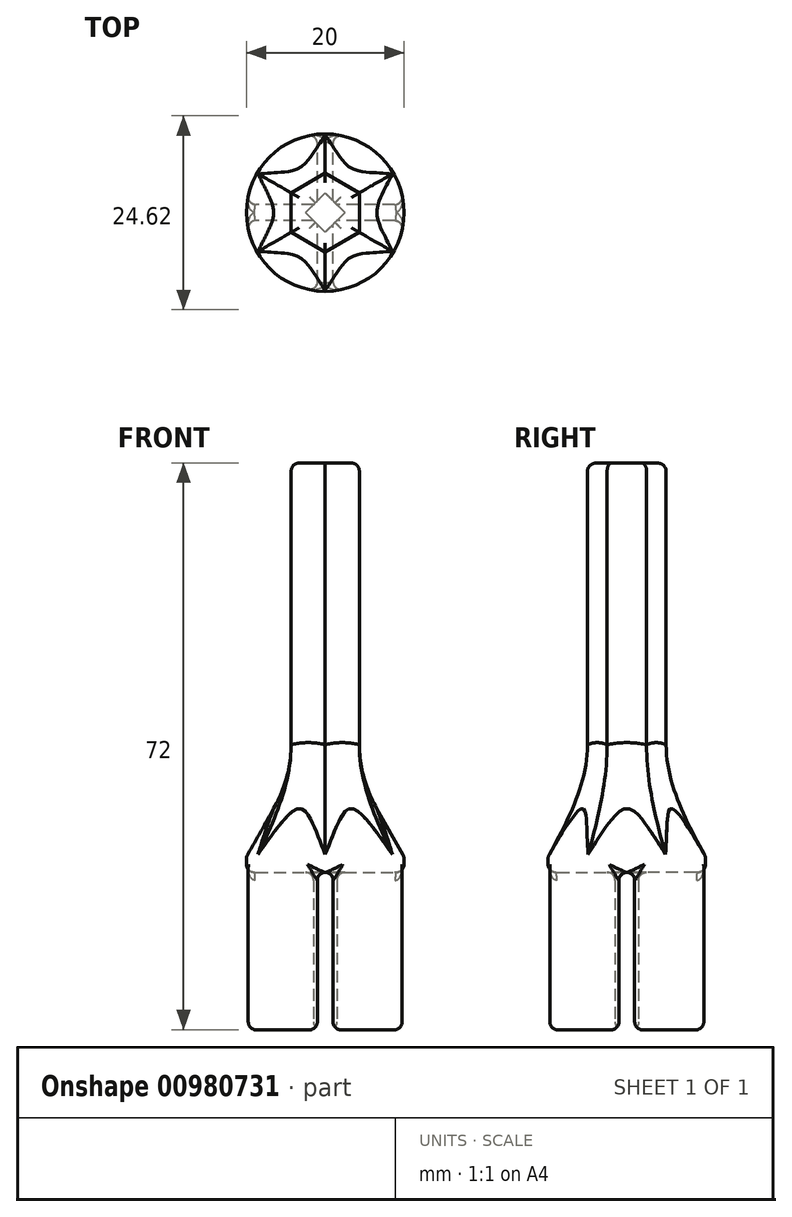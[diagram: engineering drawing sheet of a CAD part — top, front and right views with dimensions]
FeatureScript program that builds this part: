
annotation { "Feature Type Name" : "Feature", "Feature Type Description" : "" }
export const myFeature = defineFeature(function(context is Context, id is Id, definition is map)
    precondition{}
    {
        {
            var Q0;
            Q0=qCreatedBy(makeId("Top.planeOp"),FACE);
            var sketch = newSketch(context, id + "F0", { "sketchPlane" : qUnion([Q0])});
            skCircle(sketch, "E0", {"center": v(0, 0) * mm, "radius": 10 * mm});
            skLineSegment(sketch, "E1.bottom", {"start": v(15, -1) * mm, "end": v(1.5, -1) * mm});
            skLineSegment(sketch, "E1.top", {"start": v(15, 1) * mm, "end": v(1.5, 1) * mm});
            skLineSegment(sketch, "E1.left", {"start": v(15, -1) * mm, "end": v(15, 1) * mm});
            skLineSegment(sketch, "E1.right", {"start": v(-15, -1) * mm, "end": v(-15, 1) * mm});
            skLineSegment(sketch, "E2.bottom", {"start": v(1, -15) * mm, "end": v(-1, -15) * mm});
            skLineSegment(sketch, "E2.top", {"start": v(1, 15) * mm, "end": v(-1, 15) * mm});
            skLineSegment(sketch, "E2.left", {"start": v(1, -15) * mm, "end": v(1, -1.5) * mm});
            skLineSegment(sketch, "E2.right", {"start": v(-1, -15) * mm, "end": v(-1, -1.5) * mm});
            skLineSegment(sketch, "E3.bottom", {"start": v(1.5, -1.5) * mm, "end": v(-1.5, -1.5) * mm, "construction": true});
            skLineSegment(sketch, "E3.top", {"start": v(1.5, 1.5) * mm, "end": v(-1.5, 1.5) * mm, "construction": true});
            skLineSegment(sketch, "E3.left", {"start": v(1.5, -1.5) * mm, "end": v(1.5, 1.5) * mm, "construction": true});
            skLineSegment(sketch, "E3.right", {"start": v(-1.5, -1.5) * mm, "end": v(-1.5, 1.5) * mm, "construction": true});
            skLineSegment(sketch, "E4", {"start": v(1.5, 1) * mm, "end": v(-1.5, 1) * mm, "construction": true});
            skLineSegment(sketch, "E5", {"start": v(1, 1.5) * mm, "end": v(1, 15) * mm});
            skLineSegment(sketch, "E6", {"start": v(-1, 1.5) * mm, "end": v(-1, 15) * mm});
            skLineSegment(sketch, "E7", {"start": v(-1.5, 1) * mm, "end": v(-15, 1) * mm});
            skLineSegment(sketch, "E8", {"start": v(-1.5, -1) * mm, "end": v(-15, -1) * mm});
            skLineSegment(sketch, "E9", {"start": v(-1, -1.5) * mm, "end": v(-1, 1.5) * mm, "construction": true});
            skLineSegment(sketch, "E10", {"start": v(1, -1.5) * mm, "end": v(1, 1.5) * mm, "construction": true});
            skLineSegment(sketch, "E11", {"start": v(1.5, -1) * mm, "end": v(-1.5, -1) * mm, "construction": true});
            skLineSegment(sketch, "E12", {"start": v(-1.5, -1) * mm, "end": v(-1, -1.5) * mm});
            skLineSegment(sketch, "E13", {"start": v(1, -1.5) * mm, "end": v(1.5, -1) * mm});
            skLineSegment(sketch, "E14", {"start": v(1.5, 1) * mm, "end": v(1, 1.5) * mm});
            skLineSegment(sketch, "E15", {"start": v(-1, 1.5) * mm, "end": v(-1.5, 1) * mm});
            skSolve(sketch);
        }
        {
            var Q0;
            {var subQ5=sQuery(id+"F0.wireOp",EDGE,"E13");Q0=makeQuery(id+"F0.imprint","IMPRINT",FACE,{"disambiguationData":[TD([[makeQuery(id+"F0.imprint","IMPRINT",EDGE,{"derivedFrom":subQ5}),-1.0]])]});}
            var Q1;
            {var subQ5=sQuery(id+"F0.wireOp",EDGE,"E14");Q1=makeQuery(id+"F0.imprint","IMPRINT",FACE,{"disambiguationData":[TD([[makeQuery(id+"F0.imprint","IMPRINT",EDGE,{"derivedFrom":subQ5}),-1.0]])]});}
            var Q2;
            {var subQ5=sQuery(id+"F0.wireOp",EDGE,"E15");Q2=makeQuery(id+"F0.imprint","IMPRINT",FACE,{"disambiguationData":[TD([[makeQuery(id+"F0.imprint","IMPRINT",EDGE,{"derivedFrom":subQ5}),-1.0]])]});}
            var Q3;
            {var subQ0=sQuery(id+"F0.wireOp",EDGE,"E12");Q3=makeQuery(id+"F0.imprint","IMPRINT",FACE,{"disambiguationData":[TD([[makeQuery(id+"F0.imprint","IMPRINT",EDGE,{"derivedFrom":subQ0}),1.0]])]});}
            var Q4;
            {var subQ5=sQuery(id+"F0.wireOp",EDGE,"E12");Q4=makeQuery(id+"F0.imprint","IMPRINT",FACE,{"disambiguationData":[TD([[makeQuery(id+"F0.imprint","IMPRINT",EDGE,{"derivedFrom":subQ5}),-1.0]])]});}
            extrude(context, id + "F1", {"entities" : qUnion([Q0, Q1, Q2, Q3, Q4]), "depth" : 22 * mm, "offsetDistance" : 25 * mm});
        }
        {
            var Q0;
            {var subQ5=sQuery(id+"F0.wireOp",EDGE,"E1.left");Q0=makeQuery(id+"F0.imprint","IMPRINT",FACE,{"disambiguationData":[TD([[makeQuery(id+"F0.imprint","IMPRINT",EDGE,{"derivedFrom":subQ5}),1.0]])]});}
            var Q1;
            {var subQ5=sQuery(id+"F0.wireOp",EDGE,"E2.top");Q1=makeQuery(id+"F0.imprint","IMPRINT",FACE,{"disambiguationData":[TD([[makeQuery(id+"F0.imprint","IMPRINT",EDGE,{"derivedFrom":subQ5}),1.0]])]});}
            var Q2;
            {var subQ5=sQuery(id+"F0.wireOp",EDGE,"E1.right");Q2=makeQuery(id+"F0.imprint","IMPRINT",FACE,{"disambiguationData":[TD([[makeQuery(id+"F0.imprint","IMPRINT",EDGE,{"derivedFrom":subQ5}),-1.0]])]});}
            var Q3;
            {var subQ0=sQuery(id+"F0.wireOp",EDGE,"E12");Q3=makeQuery(id+"F0.imprint","IMPRINT",FACE,{"disambiguationData":[TD([[makeQuery(id+"F0.imprint","IMPRINT",EDGE,{"derivedFrom":subQ0}),1.0]])]});}
            var Q4;
            {var subQ5=sQuery(id+"F0.wireOp",EDGE,"E2.bottom");Q4=makeQuery(id+"F0.imprint","IMPRINT",FACE,{"disambiguationData":[TD([[makeQuery(id+"F0.imprint","IMPRINT",EDGE,{"derivedFrom":subQ5}),-1.0]])]});}
            extrude(context, id + "F2", {"entities" : qUnion([Q0, Q1, Q2, Q3, Q4]), "operationType" : NewBodyOperationType.REMOVE, "depth" : 20 * mm, "offsetDistance" : 25 * mm});
        }
        {
            var Q0;
            Q0=qCreatedBy(makeId("Top.planeOp"),FACE);
            cPlane(context, id + "F3", {"entities" : qUnion([Q0]), "cplaneType" : CPlaneType.OFFSET, "offset" : 32 * mm, "width" : 150 * mm, "height" : 150 * mm});
        }
        {
            var Q0;
            Q0=qCreatedBy(id+"F3.planeOp",FACE);
            var sketch = newSketch(context, id + "F4", { "sketchPlane" : qUnion([Q0])});
            skCircle(sketch, "E16.cCircle", {"center": v(0, 0) * mm, "radius": 5 * mm, "construction": true});
            skLineSegment(sketch, "E16.0", {"start": v(0, 5) * mm, "end": v(4.33, 2.5) * mm});
            skLineSegment(sketch, "E16.1", {"start": v(4.33, 2.5) * mm, "end": v(4.33, -2.5) * mm});
            skLineSegment(sketch, "E16.2", {"start": v(4.33, -2.5) * mm, "end": v(0, -5) * mm});
            skLineSegment(sketch, "E16.3", {"start": v(0, -5) * mm, "end": v(-4.33, -2.5) * mm});
            skLineSegment(sketch, "E16.4", {"start": v(-4.33, -2.5) * mm, "end": v(-4.33, 2.5) * mm});
            skLineSegment(sketch, "E16.5", {"start": v(-4.33, 2.5) * mm, "end": v(0, 5) * mm});
            skCircle(sketch, "E17", {"center": v(0, 0) * mm, "radius": 4.33 * mm});
            skSolve(sketch);
        }
        {
            var Q0;
            {var subQ0=sQuery(id+"F4.wireOp",EDGE,"E17");var subQ4=makeQuery(id+"F4.imprint","INTERSECT",VERTEX,{"derivedFrom":[sQuery(id+"F4.wireOp",EDGE,"E16.0"),subQ0]});Q0=makeQuery(id+"F4.imprint","IMPRINT",FACE,{"disambiguationData":[TD([[makeQuery(id+"F4.imprint","IMPRINT",EDGE,{"disambiguationData":[TD([[subQ4,1.0]])],"derivedFrom":subQ0}),1.0]])]});}
            var sketch = newSketch(context, id + "F5", { "sketchPlane" : qUnion([Q0])});
            skSolve(sketch);
        }
        {
            var Q1;
            Q1=makeQuery(id+"F1.opExtrude","CAP_FACE",FACE,{"disambiguationData":[OSD([sQuery(id+"F0.wireOp",EDGE,"E0")])],"isStart":false});
            var Q2;
            {var subQ0=sQuery(id+"F4.wireOp",EDGE,"E17");var subQ4=makeQuery(id+"F4.imprint","INTERSECT",VERTEX,{"derivedFrom":[sQuery(id+"F4.wireOp",EDGE,"E16.0"),subQ0]});Q2=makeQuery(id+"F5.imprint","IMPRINT",FACE,{"disambiguationData":[TD([[makeQuery(id+"F5.imprint","IMPRINT",EDGE,{"derivedFrom":makeQuery(id+"F4.imprint","IMPRINT",EDGE,{"disambiguationData":[TD([[subQ4,1.0]])],"derivedFrom":subQ0})}),1.0]])]});}
            loft(context, id + "F6", {"operationType" : NewBodyOperationType.ADD, "sheetProfilesArray" : [{ "sheetProfileEntities" : qUnion([Q1]) }, { "sheetProfileEntities" : qUnion([Q2]) }]});
        }
        {
            var Q0;
            {var subQ0=sQuery(id+"F4.wireOp",EDGE,"E16.4");var subQ1=sQuery(id+"F4.wireOp",EDGE,"E16.3");var subQ2=makeQuery(id+"F4.imprint","INTERSECT",VERTEX,{"derivedFrom":[subQ1,subQ0]});Q0=makeQuery(id+"F4.imprint","IMPRINT",FACE,{"disambiguationData":[TD([[makeQuery(id+"F4.imprint","IMPRINT",EDGE,{"disambiguationData":[TD([[subQ2,1.0]])],"derivedFrom":subQ1}),-1.0]])]});}
            var Q1;
            {var subQ0=sQuery(id+"F4.wireOp",EDGE,"E16.5");var subQ1=sQuery(id+"F4.wireOp",EDGE,"E16.0");var subQ2=makeQuery(id+"F4.imprint","INTERSECT",VERTEX,{"derivedFrom":[subQ1,subQ0]});Q1=makeQuery(id+"F4.imprint","IMPRINT",FACE,{"disambiguationData":[TD([[makeQuery(id+"F4.imprint","IMPRINT",EDGE,{"disambiguationData":[TD([[subQ2,-1.0]])],"derivedFrom":subQ1}),-1.0]])]});}
            var Q2;
            {var subQ0=sQuery(id+"F4.wireOp",EDGE,"E16.1");var subQ1=sQuery(id+"F4.wireOp",EDGE,"E16.0");var subQ2=makeQuery(id+"F4.imprint","INTERSECT",VERTEX,{"derivedFrom":[subQ1,subQ0]});Q2=makeQuery(id+"F4.imprint","IMPRINT",FACE,{"disambiguationData":[TD([[makeQuery(id+"F4.imprint","IMPRINT",EDGE,{"disambiguationData":[TD([[subQ2,1.0]])],"derivedFrom":subQ1}),-1.0]])]});}
            var Q3;
            {var subQ0=sQuery(id+"F4.wireOp",EDGE,"E16.3");var subQ1=sQuery(id+"F4.wireOp",EDGE,"E16.2");var subQ2=makeQuery(id+"F4.imprint","INTERSECT",VERTEX,{"derivedFrom":[subQ1,subQ0]});Q3=makeQuery(id+"F4.imprint","IMPRINT",FACE,{"disambiguationData":[TD([[makeQuery(id+"F4.imprint","IMPRINT",EDGE,{"disambiguationData":[TD([[subQ2,1.0]])],"derivedFrom":subQ1}),-1.0]])]});}
            var Q4;
            {var subQ0=sQuery(id+"F4.wireOp",EDGE,"E17");var subQ4=makeQuery(id+"F4.imprint","INTERSECT",VERTEX,{"derivedFrom":[sQuery(id+"F4.wireOp",EDGE,"E16.0"),subQ0]});Q4=makeQuery(id+"F4.imprint","IMPRINT",FACE,{"disambiguationData":[TD([[makeQuery(id+"F4.imprint","IMPRINT",EDGE,{"disambiguationData":[TD([[subQ4,1.0]])],"derivedFrom":subQ0}),1.0]])]});}
            var Q5;
            {var subQ0=sQuery(id+"F4.wireOp",EDGE,"E16.2");var subQ1=sQuery(id+"F4.wireOp",EDGE,"E16.1");var subQ2=makeQuery(id+"F4.imprint","INTERSECT",VERTEX,{"derivedFrom":[subQ1,subQ0]});Q5=makeQuery(id+"F4.imprint","IMPRINT",FACE,{"disambiguationData":[TD([[makeQuery(id+"F4.imprint","IMPRINT",EDGE,{"disambiguationData":[TD([[subQ2,1.0]])],"derivedFrom":subQ1}),-1.0]])]});}
            var Q6;
            {var subQ0=sQuery(id+"F4.wireOp",EDGE,"E16.5");var subQ1=sQuery(id+"F4.wireOp",EDGE,"E16.4");var subQ2=makeQuery(id+"F4.imprint","INTERSECT",VERTEX,{"derivedFrom":[subQ1,subQ0]});Q6=makeQuery(id+"F4.imprint","IMPRINT",FACE,{"disambiguationData":[TD([[makeQuery(id+"F4.imprint","IMPRINT",EDGE,{"disambiguationData":[TD([[subQ2,1.0]])],"derivedFrom":subQ1}),-1.0]])]});}
            extrude(context, id + "F7", {"entities" : qUnion([Q0, Q1, Q2, Q3, Q4, Q5, Q6]), "operationType" : NewBodyOperationType.ADD, "depth" : 40 * mm, "offsetDistance" : 25 * mm});
        }
        {
            var Q0;
            {var subQ0=sQuery(id+"F4.wireOp",EDGE,"E16.3");var subQ1=sQuery(id+"F4.wireOp",EDGE,"E16.2");var subQ2=makeQuery(id+"F7.opExtrude","CAP_FACE",FACE,{"disambiguationData":[OSD([sQuery(id+"F4.wireOp",EDGE,"E16.0"),sQuery(id+"F4.wireOp",EDGE,"E16.1"),subQ1,subQ0,sQuery(id+"F4.wireOp",EDGE,"E16.4"),sQuery(id+"F4.wireOp",EDGE,"E16.5")])],"isStart":true});Q0=makeQuery(id+"F7.boolean.opBoolean","SPLIT",FACE,{"disambiguationData":[TD([makeQuery(id+"F6.opLoft","SWEPT_FACE",FACE,{"disambiguationData":[OSD([sQuery(id+"F0.wireOp",EDGE,"E0"),sQuery(id+"F4.wireOp",EDGE,"E17")])]}),subQ2,makeQuery(id+"F7.opExtrude","SWEPT_FACE",FACE,{"disambiguationData":[OSD([subQ1])]}),makeQuery(id+"F7.opExtrude","SWEPT_FACE",FACE,{"disambiguationData":[OSD([subQ0])]})])],"derivedFrom":subQ2});}
            var Q1;
            {var subQ0=sQuery(id+"F4.wireOp",EDGE,"E16.1");var subQ1=sQuery(id+"F4.wireOp",EDGE,"E16.2");var subQ2=makeQuery(id+"F7.opExtrude","CAP_FACE",FACE,{"disambiguationData":[OSD([sQuery(id+"F4.wireOp",EDGE,"E16.0"),subQ0,subQ1,sQuery(id+"F4.wireOp",EDGE,"E16.3"),sQuery(id+"F4.wireOp",EDGE,"E16.4"),sQuery(id+"F4.wireOp",EDGE,"E16.5")])],"isStart":true});Q1=makeQuery(id+"F7.boolean.opBoolean","SPLIT",FACE,{"disambiguationData":[TD([makeQuery(id+"F6.opLoft","SWEPT_FACE",FACE,{"disambiguationData":[OSD([sQuery(id+"F0.wireOp",EDGE,"E0"),sQuery(id+"F4.wireOp",EDGE,"E17")])]}),subQ2,makeQuery(id+"F7.opExtrude","SWEPT_FACE",FACE,{"disambiguationData":[OSD([subQ0])]}),makeQuery(id+"F7.opExtrude","SWEPT_FACE",FACE,{"disambiguationData":[OSD([subQ1])]})])],"derivedFrom":subQ2});}
            var Q2;
            {var subQ0=sQuery(id+"F4.wireOp",EDGE,"E16.4");var subQ1=sQuery(id+"F4.wireOp",EDGE,"E16.3");var subQ2=makeQuery(id+"F7.opExtrude","CAP_FACE",FACE,{"disambiguationData":[OSD([sQuery(id+"F4.wireOp",EDGE,"E16.0"),sQuery(id+"F4.wireOp",EDGE,"E16.1"),sQuery(id+"F4.wireOp",EDGE,"E16.2"),subQ1,subQ0,sQuery(id+"F4.wireOp",EDGE,"E16.5")])],"isStart":true});Q2=makeQuery(id+"F7.boolean.opBoolean","SPLIT",FACE,{"disambiguationData":[TD([makeQuery(id+"F6.opLoft","SWEPT_FACE",FACE,{"disambiguationData":[OSD([sQuery(id+"F0.wireOp",EDGE,"E0"),sQuery(id+"F4.wireOp",EDGE,"E17")])]}),subQ2,makeQuery(id+"F7.opExtrude","SWEPT_FACE",FACE,{"disambiguationData":[OSD([subQ1])]}),makeQuery(id+"F7.opExtrude","SWEPT_FACE",FACE,{"disambiguationData":[OSD([subQ0])]})])],"derivedFrom":subQ2});}
            var Q3;
            {var subQ0=sQuery(id+"F4.wireOp",EDGE,"E16.5");var subQ1=sQuery(id+"F4.wireOp",EDGE,"E16.4");var subQ2=makeQuery(id+"F7.opExtrude","CAP_FACE",FACE,{"disambiguationData":[OSD([sQuery(id+"F4.wireOp",EDGE,"E16.0"),sQuery(id+"F4.wireOp",EDGE,"E16.1"),sQuery(id+"F4.wireOp",EDGE,"E16.2"),sQuery(id+"F4.wireOp",EDGE,"E16.3"),subQ1,subQ0])],"isStart":true});Q3=makeQuery(id+"F7.boolean.opBoolean","SPLIT",FACE,{"disambiguationData":[TD([makeQuery(id+"F6.opLoft","SWEPT_FACE",FACE,{"disambiguationData":[OSD([sQuery(id+"F0.wireOp",EDGE,"E0"),sQuery(id+"F4.wireOp",EDGE,"E17")])]}),subQ2,makeQuery(id+"F7.opExtrude","SWEPT_FACE",FACE,{"disambiguationData":[OSD([subQ1])]}),makeQuery(id+"F7.opExtrude","SWEPT_FACE",FACE,{"disambiguationData":[OSD([subQ0])]})])],"derivedFrom":subQ2});}
            var Q4;
            {var subQ0=sQuery(id+"F4.wireOp",EDGE,"E16.0");var subQ1=sQuery(id+"F4.wireOp",EDGE,"E16.5");var subQ2=makeQuery(id+"F7.opExtrude","CAP_FACE",FACE,{"disambiguationData":[OSD([subQ0,sQuery(id+"F4.wireOp",EDGE,"E16.1"),sQuery(id+"F4.wireOp",EDGE,"E16.2"),sQuery(id+"F4.wireOp",EDGE,"E16.3"),sQuery(id+"F4.wireOp",EDGE,"E16.4"),subQ1])],"isStart":true});Q4=makeQuery(id+"F7.boolean.opBoolean","SPLIT",FACE,{"disambiguationData":[TD([makeQuery(id+"F6.opLoft","SWEPT_FACE",FACE,{"disambiguationData":[OSD([sQuery(id+"F0.wireOp",EDGE,"E0"),sQuery(id+"F4.wireOp",EDGE,"E17")])]}),makeQuery(id+"F7.opExtrude","SWEPT_FACE",FACE,{"disambiguationData":[OSD([subQ0])]}),subQ2,makeQuery(id+"F7.opExtrude","SWEPT_FACE",FACE,{"disambiguationData":[OSD([subQ1])]})])],"derivedFrom":subQ2});}
            var Q5;
            {var subQ0=sQuery(id+"F4.wireOp",EDGE,"E16.1");var subQ1=sQuery(id+"F4.wireOp",EDGE,"E16.0");var subQ2=makeQuery(id+"F7.opExtrude","CAP_FACE",FACE,{"disambiguationData":[OSD([subQ1,subQ0,sQuery(id+"F4.wireOp",EDGE,"E16.2"),sQuery(id+"F4.wireOp",EDGE,"E16.3"),sQuery(id+"F4.wireOp",EDGE,"E16.4"),sQuery(id+"F4.wireOp",EDGE,"E16.5")])],"isStart":true});Q5=makeQuery(id+"F7.boolean.opBoolean","SPLIT",FACE,{"disambiguationData":[TD([makeQuery(id+"F6.opLoft","SWEPT_FACE",FACE,{"disambiguationData":[OSD([sQuery(id+"F0.wireOp",EDGE,"E0"),sQuery(id+"F4.wireOp",EDGE,"E17")])]}),makeQuery(id+"F7.opExtrude","SWEPT_FACE",FACE,{"disambiguationData":[OSD([subQ1])]}),subQ2,makeQuery(id+"F7.opExtrude","SWEPT_FACE",FACE,{"disambiguationData":[OSD([subQ0])]})])],"derivedFrom":subQ2});}
            extrude(context, id + "F8", {"entities" : qUnion([Q0, Q1, Q2, Q3, Q4, Q5]), "operationType" : NewBodyOperationType.ADD, "depth" : 2 * mm, "offsetDistance" : 25 * mm});
        }
        {
            var Q0;
            {var subQ0=makeQuery(id+"F6.opLoft","SWEPT_FACE",FACE,{"disambiguationData":[OSD([sQuery(id+"F0.wireOp",EDGE,"E0"),sQuery(id+"F4.wireOp",EDGE,"E17")])]});var subQ1=sQuery(id+"F4.wireOp",EDGE,"E16.5");var subQ2=sQuery(id+"F4.wireOp",EDGE,"E16.4");var subQ3=sQuery(id+"F4.wireOp",EDGE,"E16.0");var subQ6=makeQuery(id+"F7.opExtrude","CAP_EDGE",EDGE,{"disambiguationData":[OSD([subQ1])],"isStart":true});Q0=makeQuery(id+"F8.boolean.opBoolean","INTERSECT",EDGE,{"derivedFrom":[subQ0,makeQuery(id+"F8.opExtrude","SWEPT_FACE",FACE,{"disambiguationData":[OSD([subQ1]),TDD([makeQuery(id+"F7.boolean.opBoolean","SPLIT",EDGE,{"disambiguationData":[TD([makeQuery(id+"F7.opExtrude","SWEPT_FACE",FACE,{"disambiguationData":[OSD([subQ3])]})])],"derivedFrom":subQ6})])]}),makeQuery(id+"F8.opExtrude","SWEPT_FACE",FACE,{"disambiguationData":[OSD([subQ1]),TDD([makeQuery(id+"F7.boolean.opBoolean","SPLIT",EDGE,{"disambiguationData":[TD([makeQuery(id+"F7.opExtrude","SWEPT_FACE",FACE,{"disambiguationData":[OSD([subQ2])]})])],"derivedFrom":subQ6})])]})]});}
            var Q1;
            {var subQ0=makeQuery(id+"F6.opLoft","SWEPT_FACE",FACE,{"disambiguationData":[OSD([sQuery(id+"F0.wireOp",EDGE,"E0"),sQuery(id+"F4.wireOp",EDGE,"E17")])]});var subQ1=sQuery(id+"F4.wireOp",EDGE,"E16.5");var subQ2=sQuery(id+"F4.wireOp",EDGE,"E16.4");var subQ3=sQuery(id+"F4.wireOp",EDGE,"E16.3");var subQ6=makeQuery(id+"F7.opExtrude","CAP_EDGE",EDGE,{"disambiguationData":[OSD([subQ2])],"isStart":true});Q1=makeQuery(id+"F8.boolean.opBoolean","INTERSECT",EDGE,{"derivedFrom":[subQ0,makeQuery(id+"F8.opExtrude","SWEPT_FACE",FACE,{"disambiguationData":[OSD([subQ2]),TDD([makeQuery(id+"F7.boolean.opBoolean","SPLIT",EDGE,{"disambiguationData":[TD([makeQuery(id+"F7.opExtrude","SWEPT_FACE",FACE,{"disambiguationData":[OSD([subQ3])]})])],"derivedFrom":subQ6})])]}),makeQuery(id+"F8.opExtrude","SWEPT_FACE",FACE,{"disambiguationData":[OSD([subQ2]),TDD([makeQuery(id+"F7.boolean.opBoolean","SPLIT",EDGE,{"disambiguationData":[TD([makeQuery(id+"F7.opExtrude","SWEPT_FACE",FACE,{"disambiguationData":[OSD([subQ1])]})])],"derivedFrom":subQ6})])]})]});}
            var Q2;
            {var subQ0=makeQuery(id+"F6.opLoft","SWEPT_FACE",FACE,{"disambiguationData":[OSD([sQuery(id+"F0.wireOp",EDGE,"E0"),sQuery(id+"F4.wireOp",EDGE,"E17")])]});var subQ1=sQuery(id+"F4.wireOp",EDGE,"E16.3");var subQ2=sQuery(id+"F4.wireOp",EDGE,"E16.2");var subQ3=sQuery(id+"F4.wireOp",EDGE,"E16.1");var subQ6=makeQuery(id+"F7.opExtrude","CAP_EDGE",EDGE,{"disambiguationData":[OSD([subQ2])],"isStart":true});Q2=makeQuery(id+"F8.boolean.opBoolean","INTERSECT",EDGE,{"derivedFrom":[subQ0,makeQuery(id+"F8.opExtrude","SWEPT_FACE",FACE,{"disambiguationData":[OSD([subQ2]),TDD([makeQuery(id+"F7.boolean.opBoolean","SPLIT",EDGE,{"disambiguationData":[TD([makeQuery(id+"F7.opExtrude","SWEPT_FACE",FACE,{"disambiguationData":[OSD([subQ3])]})])],"derivedFrom":subQ6})])]}),makeQuery(id+"F8.opExtrude","SWEPT_FACE",FACE,{"disambiguationData":[OSD([subQ2]),TDD([makeQuery(id+"F7.boolean.opBoolean","SPLIT",EDGE,{"disambiguationData":[TD([makeQuery(id+"F7.opExtrude","SWEPT_FACE",FACE,{"disambiguationData":[OSD([subQ1])]})])],"derivedFrom":subQ6})])]})]});}
            var Q3;
            {var subQ0=makeQuery(id+"F6.opLoft","SWEPT_FACE",FACE,{"disambiguationData":[OSD([sQuery(id+"F0.wireOp",EDGE,"E0"),sQuery(id+"F4.wireOp",EDGE,"E17")])]});var subQ1=sQuery(id+"F4.wireOp",EDGE,"E16.1");var subQ2=sQuery(id+"F4.wireOp",EDGE,"E16.0");var subQ4=sQuery(id+"F4.wireOp",EDGE,"E16.5");var subQ6=makeQuery(id+"F7.opExtrude","CAP_EDGE",EDGE,{"disambiguationData":[OSD([subQ2])],"isStart":true});Q3=makeQuery(id+"F8.boolean.opBoolean","INTERSECT",EDGE,{"derivedFrom":[subQ0,makeQuery(id+"F8.opExtrude","SWEPT_FACE",FACE,{"disambiguationData":[OSD([subQ2]),TDD([makeQuery(id+"F7.boolean.opBoolean","SPLIT",EDGE,{"disambiguationData":[TD([makeQuery(id+"F7.opExtrude","SWEPT_FACE",FACE,{"disambiguationData":[OSD([subQ4])]})])],"derivedFrom":subQ6})])]}),makeQuery(id+"F8.opExtrude","SWEPT_FACE",FACE,{"disambiguationData":[OSD([subQ2]),TDD([makeQuery(id+"F7.boolean.opBoolean","SPLIT",EDGE,{"disambiguationData":[TD([makeQuery(id+"F7.opExtrude","SWEPT_FACE",FACE,{"disambiguationData":[OSD([subQ1])]})])],"derivedFrom":subQ6})])]})]});}
            var Q4;
            {var subQ0=makeQuery(id+"F6.opLoft","SWEPT_FACE",FACE,{"disambiguationData":[OSD([sQuery(id+"F0.wireOp",EDGE,"E0"),sQuery(id+"F4.wireOp",EDGE,"E17")])]});var subQ1=sQuery(id+"F4.wireOp",EDGE,"E16.1");var subQ3=sQuery(id+"F4.wireOp",EDGE,"E16.2");var subQ4=sQuery(id+"F4.wireOp",EDGE,"E16.0");var subQ6=makeQuery(id+"F7.opExtrude","CAP_EDGE",EDGE,{"disambiguationData":[OSD([subQ1])],"isStart":true});Q4=makeQuery(id+"F8.boolean.opBoolean","INTERSECT",EDGE,{"derivedFrom":[subQ0,makeQuery(id+"F8.opExtrude","SWEPT_FACE",FACE,{"disambiguationData":[OSD([subQ1]),TDD([makeQuery(id+"F7.boolean.opBoolean","SPLIT",EDGE,{"disambiguationData":[TD([makeQuery(id+"F7.opExtrude","SWEPT_FACE",FACE,{"disambiguationData":[OSD([subQ4])]})])],"derivedFrom":subQ6})])]}),makeQuery(id+"F8.opExtrude","SWEPT_FACE",FACE,{"disambiguationData":[OSD([subQ1]),TDD([makeQuery(id+"F7.boolean.opBoolean","SPLIT",EDGE,{"disambiguationData":[TD([makeQuery(id+"F7.opExtrude","SWEPT_FACE",FACE,{"disambiguationData":[OSD([subQ3])]})])],"derivedFrom":subQ6})])]})]});}
            var Q5;
            {var subQ0=makeQuery(id+"F6.opLoft","SWEPT_FACE",FACE,{"disambiguationData":[OSD([sQuery(id+"F0.wireOp",EDGE,"E0"),sQuery(id+"F4.wireOp",EDGE,"E17")])]});var subQ1=sQuery(id+"F4.wireOp",EDGE,"E16.4");var subQ2=sQuery(id+"F4.wireOp",EDGE,"E16.3");var subQ3=sQuery(id+"F4.wireOp",EDGE,"E16.2");var subQ6=makeQuery(id+"F7.opExtrude","CAP_EDGE",EDGE,{"disambiguationData":[OSD([subQ2])],"isStart":true});Q5=makeQuery(id+"F8.boolean.opBoolean","INTERSECT",EDGE,{"derivedFrom":[subQ0,makeQuery(id+"F8.opExtrude","SWEPT_FACE",FACE,{"disambiguationData":[OSD([subQ2]),TDD([makeQuery(id+"F7.boolean.opBoolean","SPLIT",EDGE,{"disambiguationData":[TD([makeQuery(id+"F7.opExtrude","SWEPT_FACE",FACE,{"disambiguationData":[OSD([subQ3])]})])],"derivedFrom":subQ6})])]}),makeQuery(id+"F8.opExtrude","SWEPT_FACE",FACE,{"disambiguationData":[OSD([subQ2]),TDD([makeQuery(id+"F7.boolean.opBoolean","SPLIT",EDGE,{"disambiguationData":[TD([makeQuery(id+"F7.opExtrude","SWEPT_FACE",FACE,{"disambiguationData":[OSD([subQ1])]})])],"derivedFrom":subQ6})])]})]});}
            fillet(context, id + "F9", {"entities" : qUnion([Q0, Q1, Q2, Q3, Q4, Q5]), "radius" : 17 * mm, "tangentPropagation" : true, "allowEdgeOverflow" : false});
        }
        {
            var Q0;
            {var subQ0=sQuery(id+"F0.wireOp",EDGE,"E0");Q0=makeQuery(id+"F2.boolean.opBoolean","SPLIT",FACE,{"disambiguationData":[TD([makeQuery(id+"F2.opExtrude","SWEPT_FACE",FACE,{"disambiguationData":[OSD([sQuery(id+"F0.wireOp",EDGE,"E1.bottom")])]})])],"derivedFrom":makeQuery(id+"F1.opExtrude","CAP_FACE",FACE,{"disambiguationData":[OSD([subQ0])],"isStart":true})});}
            var Q1;
            {var subQ0=sQuery(id+"F0.wireOp",EDGE,"E0");Q1=makeQuery(id+"F2.boolean.opBoolean","SPLIT",FACE,{"disambiguationData":[TD([makeQuery(id+"F2.opExtrude","SWEPT_FACE",FACE,{"disambiguationData":[OSD([sQuery(id+"F0.wireOp",EDGE,"E1.top")])]})])],"derivedFrom":makeQuery(id+"F1.opExtrude","CAP_FACE",FACE,{"disambiguationData":[OSD([subQ0])],"isStart":true})});}
            var Q2;
            {var subQ0=sQuery(id+"F0.wireOp",EDGE,"E0");Q2=makeQuery(id+"F2.boolean.opBoolean","SPLIT",FACE,{"disambiguationData":[TD([makeQuery(id+"F2.opExtrude","SWEPT_FACE",FACE,{"disambiguationData":[OSD([sQuery(id+"F0.wireOp",EDGE,"E6")])]})])],"derivedFrom":makeQuery(id+"F1.opExtrude","CAP_FACE",FACE,{"disambiguationData":[OSD([subQ0])],"isStart":true})});}
            var Q3;
            {var subQ0=sQuery(id+"F0.wireOp",EDGE,"E0");Q3=makeQuery(id+"F2.boolean.opBoolean","SPLIT",FACE,{"disambiguationData":[TD([makeQuery(id+"F2.opExtrude","SWEPT_FACE",FACE,{"disambiguationData":[OSD([sQuery(id+"F0.wireOp",EDGE,"E2.right")])]})])],"derivedFrom":makeQuery(id+"F1.opExtrude","CAP_FACE",FACE,{"disambiguationData":[OSD([subQ0])],"isStart":true})});}
            var Q4;
            Q4=makeQuery(id+"F1.opExtrude","SWEPT_FACE",FACE,{"disambiguationData":[OSD([sQuery(id+"F0.wireOp",EDGE,"E0")])]});
            fillet(context, id + "F10", {"entities" : qUnion([Q0, Q1, Q2, Q3, Q4]), "radius" : 1 * mm, "tangentPropagation" : true, "allowEdgeOverflow" : false});
        }
        {
            var Q0;
            {var subQ0=sQuery(id+"F0.wireOp",EDGE,"E6");var subQ1=makeQuery(id+"F1.opExtrude","SWEPT_FACE",FACE,{"disambiguationData":[OSD([sQuery(id+"F0.wireOp",EDGE,"E0")])]});Q0=makeQuery(id+"F10.opFillet","BLEND_EDGE",EDGE,{"blendedFrom":[makeQuery(id+"F2.boolean.opBoolean","INTERSECT",EDGE,{"derivedFrom":[subQ1,makeQuery(id+"F2.opExtrude","SWEPT_FACE",FACE,{"disambiguationData":[OSD([subQ0])]})]}),makeQuery(id+"F2.boolean.opBoolean","INTERSECT",EDGE,{"disambiguationData":[OD(2.0)],"derivedFrom":[subQ1,makeQuery(id+"F2.opExtrude","CAP_FACE",FACE,{"disambiguationData":[OSD([sQuery(id+"F0.wireOp",EDGE,"E1.bottom"),sQuery(id+"F0.wireOp",EDGE,"E1.top"),sQuery(id+"F0.wireOp",EDGE,"E1.left"),sQuery(id+"F0.wireOp",EDGE,"E1.right"),sQuery(id+"F0.wireOp",EDGE,"E2.bottom"),sQuery(id+"F0.wireOp",EDGE,"E2.top"),sQuery(id+"F0.wireOp",EDGE,"E2.left"),sQuery(id+"F0.wireOp",EDGE,"E2.right"),sQuery(id+"F0.wireOp",EDGE,"E5"),subQ0,sQuery(id+"F0.wireOp",EDGE,"E7"),sQuery(id+"F0.wireOp",EDGE,"E8"),sQuery(id+"F0.wireOp",EDGE,"E12"),sQuery(id+"F0.wireOp",EDGE,"E13"),sQuery(id+"F0.wireOp",EDGE,"E14"),sQuery(id+"F0.wireOp",EDGE,"E15")])],"isStart":false})]})],"blendedInto":[]});}
            var Q1;
            {var subQ0=sQuery(id+"F0.wireOp",EDGE,"E5");var subQ1=makeQuery(id+"F1.opExtrude","SWEPT_FACE",FACE,{"disambiguationData":[OSD([sQuery(id+"F0.wireOp",EDGE,"E0")])]});Q1=makeQuery(id+"F10.opFillet","BLEND_EDGE",EDGE,{"blendedFrom":[makeQuery(id+"F2.boolean.opBoolean","INTERSECT",EDGE,{"derivedFrom":[subQ1,makeQuery(id+"F2.opExtrude","SWEPT_FACE",FACE,{"disambiguationData":[OSD([subQ0])]})]}),makeQuery(id+"F2.boolean.opBoolean","INTERSECT",EDGE,{"disambiguationData":[OD(2.0)],"derivedFrom":[subQ1,makeQuery(id+"F2.opExtrude","CAP_FACE",FACE,{"disambiguationData":[OSD([sQuery(id+"F0.wireOp",EDGE,"E1.bottom"),sQuery(id+"F0.wireOp",EDGE,"E1.top"),sQuery(id+"F0.wireOp",EDGE,"E1.left"),sQuery(id+"F0.wireOp",EDGE,"E1.right"),sQuery(id+"F0.wireOp",EDGE,"E2.bottom"),sQuery(id+"F0.wireOp",EDGE,"E2.top"),sQuery(id+"F0.wireOp",EDGE,"E2.left"),sQuery(id+"F0.wireOp",EDGE,"E2.right"),subQ0,sQuery(id+"F0.wireOp",EDGE,"E6"),sQuery(id+"F0.wireOp",EDGE,"E7"),sQuery(id+"F0.wireOp",EDGE,"E8"),sQuery(id+"F0.wireOp",EDGE,"E12"),sQuery(id+"F0.wireOp",EDGE,"E13"),sQuery(id+"F0.wireOp",EDGE,"E14"),sQuery(id+"F0.wireOp",EDGE,"E15")])],"isStart":false})]})],"blendedInto":[]});}
            var Q2;
            {var subQ0=sQuery(id+"F0.wireOp",EDGE,"E1.bottom");var subQ1=makeQuery(id+"F1.opExtrude","SWEPT_FACE",FACE,{"disambiguationData":[OSD([sQuery(id+"F0.wireOp",EDGE,"E0")])]});Q2=makeQuery(id+"F10.opFillet","BLEND_EDGE",EDGE,{"blendedFrom":[makeQuery(id+"F2.boolean.opBoolean","INTERSECT",EDGE,{"derivedFrom":[subQ1,makeQuery(id+"F2.opExtrude","SWEPT_FACE",FACE,{"disambiguationData":[OSD([subQ0])]})]}),makeQuery(id+"F2.boolean.opBoolean","INTERSECT",EDGE,{"disambiguationData":[OD(0.0)],"derivedFrom":[subQ1,makeQuery(id+"F2.opExtrude","CAP_FACE",FACE,{"disambiguationData":[OSD([subQ0,sQuery(id+"F0.wireOp",EDGE,"E1.top"),sQuery(id+"F0.wireOp",EDGE,"E1.left"),sQuery(id+"F0.wireOp",EDGE,"E1.right"),sQuery(id+"F0.wireOp",EDGE,"E2.bottom"),sQuery(id+"F0.wireOp",EDGE,"E2.top"),sQuery(id+"F0.wireOp",EDGE,"E2.left"),sQuery(id+"F0.wireOp",EDGE,"E2.right"),sQuery(id+"F0.wireOp",EDGE,"E5"),sQuery(id+"F0.wireOp",EDGE,"E6"),sQuery(id+"F0.wireOp",EDGE,"E7"),sQuery(id+"F0.wireOp",EDGE,"E8"),sQuery(id+"F0.wireOp",EDGE,"E12"),sQuery(id+"F0.wireOp",EDGE,"E13"),sQuery(id+"F0.wireOp",EDGE,"E14"),sQuery(id+"F0.wireOp",EDGE,"E15")])],"isStart":false})]})],"blendedInto":[]});}
            var Q3;
            {var subQ0=sQuery(id+"F0.wireOp",EDGE,"E1.top");var subQ1=makeQuery(id+"F1.opExtrude","SWEPT_FACE",FACE,{"disambiguationData":[OSD([sQuery(id+"F0.wireOp",EDGE,"E0")])]});Q3=makeQuery(id+"F10.opFillet","BLEND_EDGE",EDGE,{"blendedFrom":[makeQuery(id+"F2.boolean.opBoolean","INTERSECT",EDGE,{"derivedFrom":[subQ1,makeQuery(id+"F2.opExtrude","SWEPT_FACE",FACE,{"disambiguationData":[OSD([subQ0])]})]}),makeQuery(id+"F2.boolean.opBoolean","INTERSECT",EDGE,{"disambiguationData":[OD(0.0)],"derivedFrom":[subQ1,makeQuery(id+"F2.opExtrude","CAP_FACE",FACE,{"disambiguationData":[OSD([sQuery(id+"F0.wireOp",EDGE,"E1.bottom"),subQ0,sQuery(id+"F0.wireOp",EDGE,"E1.left"),sQuery(id+"F0.wireOp",EDGE,"E1.right"),sQuery(id+"F0.wireOp",EDGE,"E2.bottom"),sQuery(id+"F0.wireOp",EDGE,"E2.top"),sQuery(id+"F0.wireOp",EDGE,"E2.left"),sQuery(id+"F0.wireOp",EDGE,"E2.right"),sQuery(id+"F0.wireOp",EDGE,"E5"),sQuery(id+"F0.wireOp",EDGE,"E6"),sQuery(id+"F0.wireOp",EDGE,"E7"),sQuery(id+"F0.wireOp",EDGE,"E8"),sQuery(id+"F0.wireOp",EDGE,"E12"),sQuery(id+"F0.wireOp",EDGE,"E13"),sQuery(id+"F0.wireOp",EDGE,"E14"),sQuery(id+"F0.wireOp",EDGE,"E15")])],"isStart":false})]})],"blendedInto":[]});}
            var Q4;
            {var subQ0=sQuery(id+"F0.wireOp",EDGE,"E2.left");var subQ1=makeQuery(id+"F1.opExtrude","SWEPT_FACE",FACE,{"disambiguationData":[OSD([sQuery(id+"F0.wireOp",EDGE,"E0")])]});Q4=makeQuery(id+"F10.opFillet","BLEND_EDGE",EDGE,{"blendedFrom":[makeQuery(id+"F2.boolean.opBoolean","INTERSECT",EDGE,{"derivedFrom":[subQ1,makeQuery(id+"F2.opExtrude","SWEPT_FACE",FACE,{"disambiguationData":[OSD([subQ0])]})]}),makeQuery(id+"F2.boolean.opBoolean","INTERSECT",EDGE,{"disambiguationData":[OD(1.0)],"derivedFrom":[subQ1,makeQuery(id+"F2.opExtrude","CAP_FACE",FACE,{"disambiguationData":[OSD([sQuery(id+"F0.wireOp",EDGE,"E1.bottom"),sQuery(id+"F0.wireOp",EDGE,"E1.top"),sQuery(id+"F0.wireOp",EDGE,"E1.left"),sQuery(id+"F0.wireOp",EDGE,"E1.right"),sQuery(id+"F0.wireOp",EDGE,"E2.bottom"),sQuery(id+"F0.wireOp",EDGE,"E2.top"),subQ0,sQuery(id+"F0.wireOp",EDGE,"E2.right"),sQuery(id+"F0.wireOp",EDGE,"E5"),sQuery(id+"F0.wireOp",EDGE,"E6"),sQuery(id+"F0.wireOp",EDGE,"E7"),sQuery(id+"F0.wireOp",EDGE,"E8"),sQuery(id+"F0.wireOp",EDGE,"E12"),sQuery(id+"F0.wireOp",EDGE,"E13"),sQuery(id+"F0.wireOp",EDGE,"E14"),sQuery(id+"F0.wireOp",EDGE,"E15")])],"isStart":false})]})],"blendedInto":[]});}
            var Q5;
            {var subQ0=sQuery(id+"F0.wireOp",EDGE,"E2.right");var subQ1=makeQuery(id+"F1.opExtrude","SWEPT_FACE",FACE,{"disambiguationData":[OSD([sQuery(id+"F0.wireOp",EDGE,"E0")])]});Q5=makeQuery(id+"F10.opFillet","BLEND_EDGE",EDGE,{"blendedFrom":[makeQuery(id+"F2.boolean.opBoolean","INTERSECT",EDGE,{"derivedFrom":[subQ1,makeQuery(id+"F2.opExtrude","SWEPT_FACE",FACE,{"disambiguationData":[OSD([subQ0])]})]}),makeQuery(id+"F2.boolean.opBoolean","INTERSECT",EDGE,{"disambiguationData":[OD(1.0)],"derivedFrom":[subQ1,makeQuery(id+"F2.opExtrude","CAP_FACE",FACE,{"disambiguationData":[OSD([sQuery(id+"F0.wireOp",EDGE,"E1.bottom"),sQuery(id+"F0.wireOp",EDGE,"E1.top"),sQuery(id+"F0.wireOp",EDGE,"E1.left"),sQuery(id+"F0.wireOp",EDGE,"E1.right"),sQuery(id+"F0.wireOp",EDGE,"E2.bottom"),sQuery(id+"F0.wireOp",EDGE,"E2.top"),sQuery(id+"F0.wireOp",EDGE,"E2.left"),subQ0,sQuery(id+"F0.wireOp",EDGE,"E5"),sQuery(id+"F0.wireOp",EDGE,"E6"),sQuery(id+"F0.wireOp",EDGE,"E7"),sQuery(id+"F0.wireOp",EDGE,"E8"),sQuery(id+"F0.wireOp",EDGE,"E12"),sQuery(id+"F0.wireOp",EDGE,"E13"),sQuery(id+"F0.wireOp",EDGE,"E14"),sQuery(id+"F0.wireOp",EDGE,"E15")])],"isStart":false})]})],"blendedInto":[]});}
            var Q6;
            {var subQ0=sQuery(id+"F0.wireOp",EDGE,"E8");var subQ1=makeQuery(id+"F1.opExtrude","SWEPT_FACE",FACE,{"disambiguationData":[OSD([sQuery(id+"F0.wireOp",EDGE,"E0")])]});Q6=makeQuery(id+"F10.opFillet","BLEND_EDGE",EDGE,{"blendedFrom":[makeQuery(id+"F2.boolean.opBoolean","INTERSECT",EDGE,{"derivedFrom":[subQ1,makeQuery(id+"F2.opExtrude","SWEPT_FACE",FACE,{"disambiguationData":[OSD([subQ0])]})]}),makeQuery(id+"F2.boolean.opBoolean","INTERSECT",EDGE,{"disambiguationData":[OD(3.0)],"derivedFrom":[subQ1,makeQuery(id+"F2.opExtrude","CAP_FACE",FACE,{"disambiguationData":[OSD([sQuery(id+"F0.wireOp",EDGE,"E1.bottom"),sQuery(id+"F0.wireOp",EDGE,"E1.top"),sQuery(id+"F0.wireOp",EDGE,"E1.left"),sQuery(id+"F0.wireOp",EDGE,"E1.right"),sQuery(id+"F0.wireOp",EDGE,"E2.bottom"),sQuery(id+"F0.wireOp",EDGE,"E2.top"),sQuery(id+"F0.wireOp",EDGE,"E2.left"),sQuery(id+"F0.wireOp",EDGE,"E2.right"),sQuery(id+"F0.wireOp",EDGE,"E5"),sQuery(id+"F0.wireOp",EDGE,"E6"),sQuery(id+"F0.wireOp",EDGE,"E7"),subQ0,sQuery(id+"F0.wireOp",EDGE,"E12"),sQuery(id+"F0.wireOp",EDGE,"E13"),sQuery(id+"F0.wireOp",EDGE,"E14"),sQuery(id+"F0.wireOp",EDGE,"E15")])],"isStart":false})]})],"blendedInto":[]});}
            var Q7;
            {var subQ0=sQuery(id+"F0.wireOp",EDGE,"E7");var subQ1=makeQuery(id+"F1.opExtrude","SWEPT_FACE",FACE,{"disambiguationData":[OSD([sQuery(id+"F0.wireOp",EDGE,"E0")])]});Q7=makeQuery(id+"F10.opFillet","BLEND_EDGE",EDGE,{"blendedFrom":[makeQuery(id+"F2.boolean.opBoolean","INTERSECT",EDGE,{"derivedFrom":[subQ1,makeQuery(id+"F2.opExtrude","SWEPT_FACE",FACE,{"disambiguationData":[OSD([subQ0])]})]}),makeQuery(id+"F2.boolean.opBoolean","INTERSECT",EDGE,{"disambiguationData":[OD(3.0)],"derivedFrom":[subQ1,makeQuery(id+"F2.opExtrude","CAP_FACE",FACE,{"disambiguationData":[OSD([sQuery(id+"F0.wireOp",EDGE,"E1.bottom"),sQuery(id+"F0.wireOp",EDGE,"E1.top"),sQuery(id+"F0.wireOp",EDGE,"E1.left"),sQuery(id+"F0.wireOp",EDGE,"E1.right"),sQuery(id+"F0.wireOp",EDGE,"E2.bottom"),sQuery(id+"F0.wireOp",EDGE,"E2.top"),sQuery(id+"F0.wireOp",EDGE,"E2.left"),sQuery(id+"F0.wireOp",EDGE,"E2.right"),sQuery(id+"F0.wireOp",EDGE,"E5"),sQuery(id+"F0.wireOp",EDGE,"E6"),subQ0,sQuery(id+"F0.wireOp",EDGE,"E8"),sQuery(id+"F0.wireOp",EDGE,"E12"),sQuery(id+"F0.wireOp",EDGE,"E13"),sQuery(id+"F0.wireOp",EDGE,"E14"),sQuery(id+"F0.wireOp",EDGE,"E15")])],"isStart":false})]})],"blendedInto":[]});}
            fillet(context, id + "F11", {"entities" : qUnion([Q0, Q1, Q2, Q3, Q4, Q5, Q6, Q7]), "radius" : 1 * mm, "tangentPropagation" : true, "allowEdgeOverflow" : false});
        }
        {
            var Q0;
            Q0=makeQuery(id+"F7.opExtrude","CAP_FACE",FACE,{"disambiguationData":[OSD([sQuery(id+"F4.wireOp",EDGE,"E16.0"),sQuery(id+"F4.wireOp",EDGE,"E16.1"),sQuery(id+"F4.wireOp",EDGE,"E16.2"),sQuery(id+"F4.wireOp",EDGE,"E16.3"),sQuery(id+"F4.wireOp",EDGE,"E16.4"),sQuery(id+"F4.wireOp",EDGE,"E16.5")])],"isStart":false});
            fillet(context, id + "F12", {"entities" : qUnion([Q0]), "radius" : 1 * mm, "tangentPropagation" : true, "allowEdgeOverflow" : false});
        }
    });
